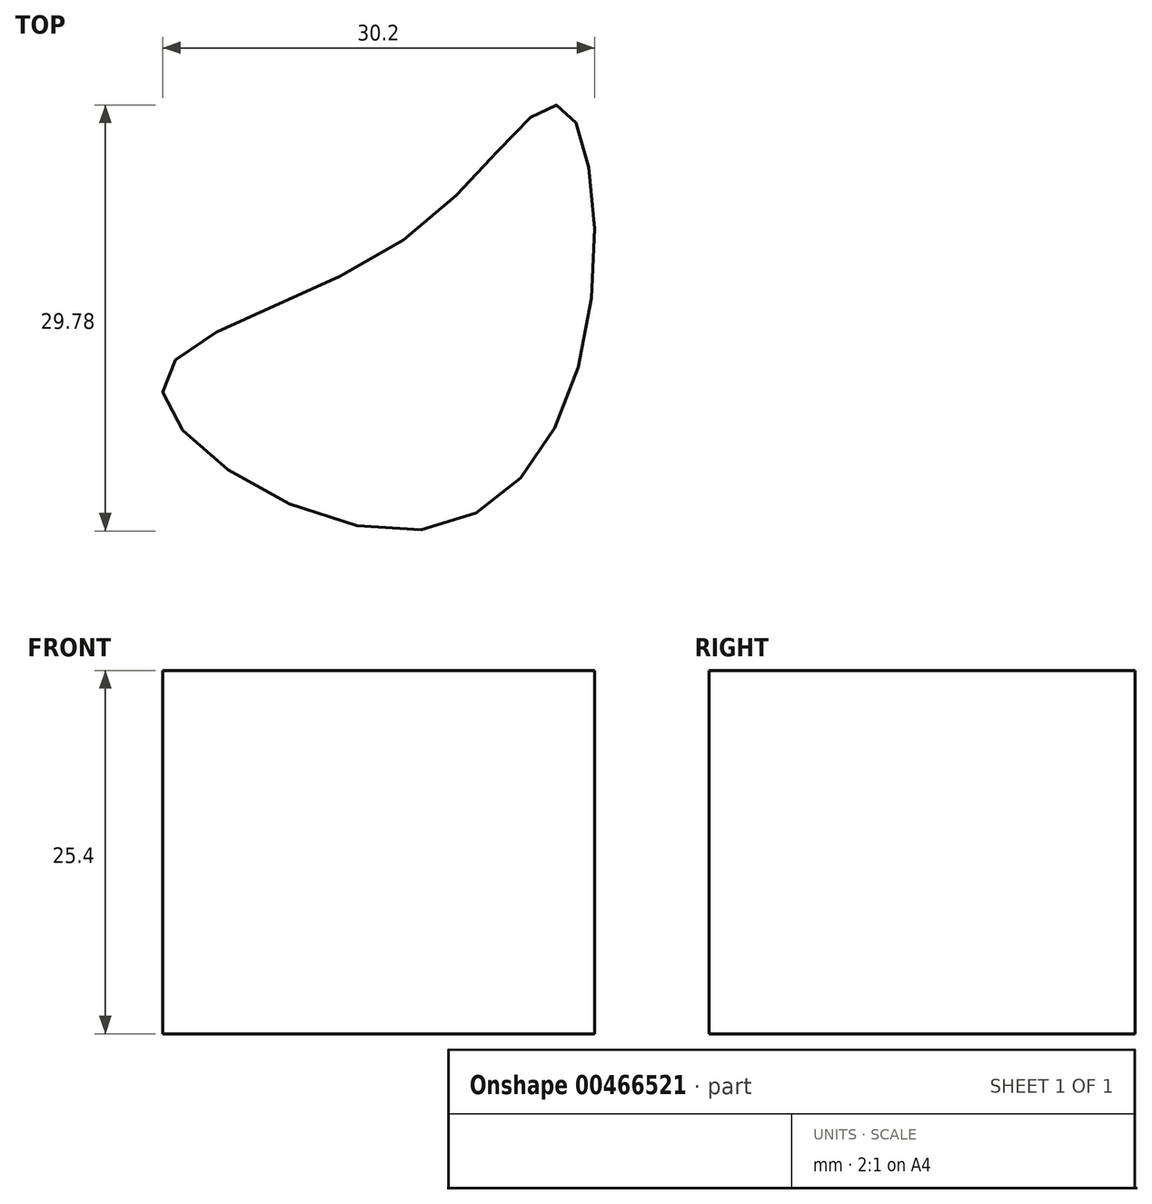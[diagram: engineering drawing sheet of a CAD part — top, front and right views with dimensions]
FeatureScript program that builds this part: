
annotation { "Feature Type Name" : "Feature", "Feature Type Description" : "" }
export const myFeature = defineFeature(function(context is Context, id is Id, definition is map)
    precondition{}
    {
        {
            var Q0;
            Q0=qCreatedBy(makeId("Top.planeOp"),FACE);
            var sketch = newSketch(context, id + "F0", { "sketchPlane" : qUnion([Q0])});
            skFitSpline(sketch, "E0", {"points": [v(0, 31.48) * mm, v(10.93, 40.88) * mm, v(12.68, 24.48) * mm, v(0, 11.15) * mm, v(-16.83, 21.2) * mm, v(0, 31.48) * mm]});
            skSolve(sketch);
        }
        {
            var Q0;
            Q0=makeQuery(id+"F0.imprint","IMPRINT",FACE,{"disambiguationData":[TD([[makeQuery(id+"F0.imprint","IMPRINT",EDGE,{"derivedFrom":sQuery(id+"F0.wireOp",EDGE,"E0")}),-1.0]])]});
            extrude(context, id + "F1", {"entities" : qUnion([Q0]), "depth" : 25.4 * mm});
        }
    });
